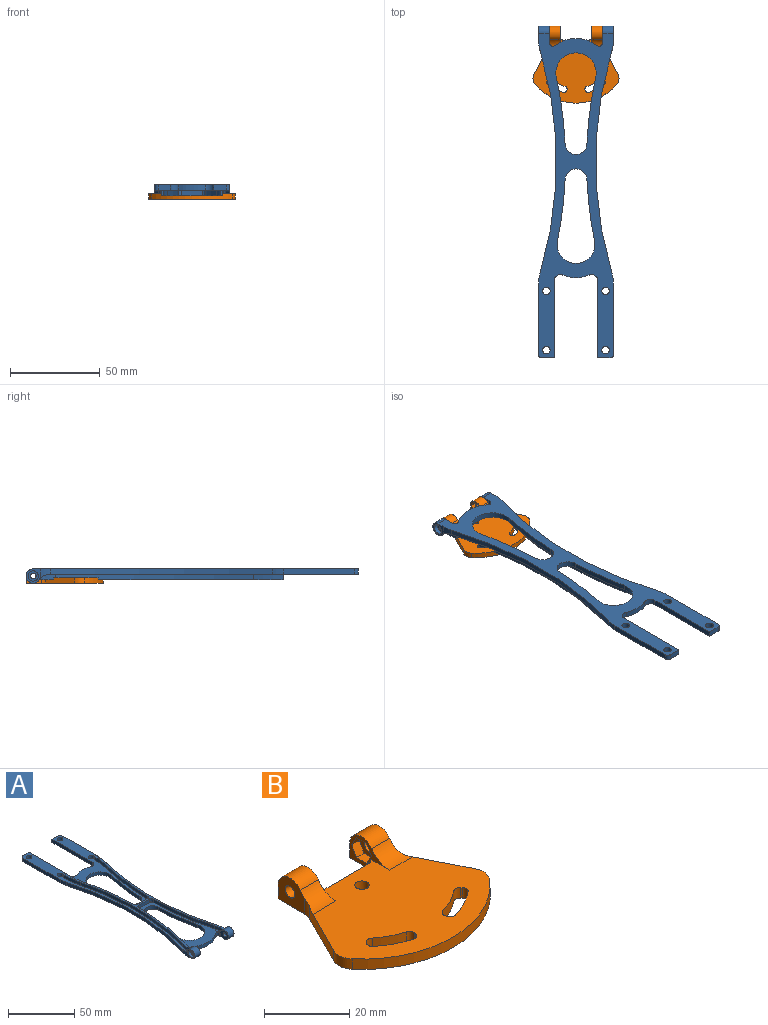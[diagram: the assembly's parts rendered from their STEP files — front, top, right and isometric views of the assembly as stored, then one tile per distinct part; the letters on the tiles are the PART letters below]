
ASSEMBLY  parts=2 mates=1
PART A: 78 faces, bbox 41.7x185x8 mm
  f0: plane 171.78x41.7mm, normal (0,0,1), area 1732.8mm2, adj f7,f8,f9,f10,f16,f17,f18,f19
  f1: plane 8x8mm, normal (-1,0,0), area 28.3mm2, adj f5,f10,f38,f43,f73
  f2: plane 13.22x8mm, normal (1,0,0), area 49.6mm2, adj f5,f6,f11,f38,f43,f71
  f3: plane 13.22x8mm, normal (-1,0,0), area 49.6mm2, adj f5,f6,f15,f37,f44,f68
  f4: plane 8x8mm, normal (1,0,0), area 28.3mm2, adj f5,f16,f37,f44,f70
  f5: plane 181x41.7mm, normal (0,0,-1), area 2806.4mm2, adj f1,f2,f3,f4,f7,f8,f9,f10
  f6: plane 67.94x33.25mm, normal (0,0,1), area 544.7mm2, adj f2,f3,f11,f12,f13,f14,f15,f31
  f7: cylinder r=6.08mm len=12.14mm, axis (0,0,-1), area 55.6mm2, adj f0,f5,f8,f36
  f8: cylinder r=218.83mm len=34.19mm, axis (0,0,-1), area 103.5mm2, adj f0,f5,f7,f9
  f9: cylinder r=10.53mm len=21.07mm, axis (0,0,-1), area 112.1mm2, adj f0,f5,f8,f36
  f10: cylinder r=20mm len=5.79mm, axis (0,0,-1), area 21.4mm2, adj f0,f1,f5,f34,f43
  f11: cylinder r=39.51mm len=3mm, axis (0,0,-1), area 4.1mm2, adj f2,f5,f6,f12
  f12: cylinder r=2mm len=3.21mm, axis (0,0,-1), area 13.1mm2, adj f5,f6,f11,f13
  f13: cylinder r=19.23mm len=23.27mm, axis (0,0,-1), area 75mm2, adj f5,f6,f12,f14
  f14: cylinder r=2mm len=3.21mm, axis (0,0,-1), area 13.1mm2, adj f5,f6,f13,f15
  f15: cylinder r=39.51mm len=3mm, axis (0,0,-1), area 4.1mm2, adj f3,f5,f6,f14
  f16: cylinder r=20mm len=5.79mm, axis (0,0,-1), area 21.4mm2, adj f0,f4,f5,f17,f44
  f17: cylinder r=213.83mm len=123.73mm, axis (0,0,-1), area 376.6mm2, adj f0,f5,f16,f18
  f18: cylinder r=20mm len=5.79mm, axis (0,0,-1), area 17.6mm2, adj f0,f5,f17,f19
  f19: plane 39.8x3mm, normal (1,0,0), area 119.4mm2, adj f0,f5,f18,f20
  f20: cylinder r=1.9mm len=3mm, axis (0,0,-1), area 9mm2, adj f0,f5,f19,f21
  f21: plane 6.8x3mm, normal (0,1,0), area 20.4mm2, adj f0,f5,f20,f22
  f22: plane 42.97x3mm, normal (-1,0,0), area 128.9mm2, adj f0,f5,f21,f23
  f23: cylinder r=3.5mm len=4.87mm, axis (0,0,-1), area 20.7mm2, adj f0,f5,f22,f24
  f24: cylinder r=18.53mm len=14.55mm, axis (0,0,-1), area 44.9mm2, adj f0,f5,f23,f25
  f25: cylinder r=3.5mm len=4.87mm, axis (0,0,-1), area 20.7mm2, adj f0,f5,f24,f26
  f26: plane 42.97x3mm, normal (1,0,0), area 128.9mm2, adj f0,f5,f25,f27
  f27: plane 6.8x3mm, normal (0,1,0), area 20.4mm2, adj f0,f5,f26,f28
  f28: cylinder r=1.9mm len=3mm, axis (0,0,-1), area 9mm2, adj f0,f5,f27,f29
  f29: plane 39.8x3mm, normal (-1,0,0), area 119.4mm2, adj f0,f5,f28,f30
  f30: cylinder r=20mm len=5.79mm, axis (0,0,-1), area 17.6mm2, adj f0,f5,f29,f34
  f31: cylinder r=6.08mm len=12.14mm, axis (0,0,-1), area 55.6mm2, adj f5,f6,f32,f35
  f32: cylinder r=218.83mm len=37.24mm, axis (0,0,-1), area 112.8mm2, adj f5,f6,f31,f33
  f33: cylinder r=11.23mm len=22.46mm, axis (0,0,-1), area 120.4mm2, adj f5,f6,f32,f35
  f34: cylinder r=213.83mm len=123.73mm, axis (0,0,-1), area 376.6mm2, adj f0,f5,f10,f30
  f35: cylinder r=218.83mm len=37.24mm, axis (0,0,-1), area 112.8mm2, adj f5,f6,f31,f33
  f36: cylinder r=218.83mm len=34.19mm, axis (0,0,-1), area 103.5mm2, adj f0,f5,f7,f9
  f37: cylinder r=4mm len=8mm, axis (1,0,0), area 99mm2, adj f3,f4,f5,f44
  f38: cylinder r=4mm len=8mm, axis (1,0,0), area 99mm2, adj f1,f2,f5,f43
  f39: cylinder r=2.1mm len=4.2mm, axis (0,0,-1), area 39.6mm2, adj f0,f5
  f40: cylinder r=2.1mm len=4.2mm, axis (0,0,-1), area 39.6mm2, adj f0,f5
  f41: cylinder r=2.1mm len=4.2mm, axis (0,0,-1), area 39.6mm2, adj f0,f5
  f42: cylinder r=2.1mm len=4.2mm, axis (0,0,-1), area 39.6mm2, adj f0,f5
  f43: cylinder r=7mm len=5.99mm, axis (1,0,0), area 30.3mm2, adj f0,f1,f2,f6,f10,f38,f45,f46
  f44: cylinder r=7mm len=5.99mm, axis (1,0,0), area 30.3mm2, adj f0,f3,f4,f6,f16,f37,f47,f48
  f45: plane 0.66x0.53mm, normal (-1,0,0), area 0.2mm2, adj f43,f47,f61
  f46: plane 0.66x0.53mm, normal (1,0,0), area 0.2mm2, adj f43,f47,f64
  f47: plane 135.83x37.22mm, normal (0,0,1), area 438.3mm2, adj f43,f44,f45,f46,f48,f49,f50,f51
  f48: plane 0.66x0.53mm, normal (-1,0,0), area 0.2mm2, adj f44,f47,f53
  f49: plane 0.66x0.53mm, normal (1,0,0), area 0.2mm2, adj f44,f47,f56
  f50: cylinder r=217.08mm len=48.83mm, axis (0,0,1), area 148mm2, adj f0,f47,f54,f75
  f51: plane 3x1.5mm, normal (0,1,0), area 4.5mm2, adj f0,f47,f54,f57
  f52: cylinder r=217.08mm len=57.11mm, axis (0,0,1), area 173.7mm2, adj f6,f47,f53,f74
  f53: cylinder r=28.36mm len=7.82mm, axis (0,0,1), area 20mm2, adj f6,f44,f47,f48,f52
  f54: cylinder r=67.77mm len=16.09mm, axis (0,0,1), area 48.7mm2, adj f0,f47,f50,f51
  f55: cylinder r=215.58mm len=110.62mm, axis (0,0,1), area 335.7mm2, adj f0,f47,f56,f57
  f56: cylinder r=29.86mm len=8.23mm, axis (0,0,1), area 21.3mm2, adj f0,f44,f47,f49,f55
  f57: cylinder r=69.27mm len=16.45mm, axis (0,0,1), area 49.8mm2, adj f0,f47,f51,f55
  f58: cylinder r=217.08mm len=48.83mm, axis (0,0,1), area 148mm2, adj f0,f47,f65,f77
  f59: plane 3x1.5mm, normal (0,1,0), area 4.5mm2, adj f0,f47,f62,f65
  f60: cylinder r=215.58mm len=110.62mm, axis (0,0,1), area 335.7mm2, adj f0,f47,f61,f62
  f61: cylinder r=29.86mm len=8.23mm, axis (0,0,1), area 21.3mm2, adj f0,f43,f45,f47,f60
  f62: cylinder r=69.27mm len=16.45mm, axis (0,0,1), area 49.8mm2, adj f0,f47,f59,f60
  f63: cylinder r=217.08mm len=57.11mm, axis (0,0,1), area 173.7mm2, adj f6,f47,f64,f76
  f64: cylinder r=28.36mm len=7.82mm, axis (0,0,1), area 20mm2, adj f6,f43,f46,f47,f63
  f65: cylinder r=67.77mm len=16.09mm, axis (0,0,1), area 48.7mm2, adj f0,f47,f58,f59
  f66: plane 11.23x3mm, normal (0,-1,0), area 33.7mm2, adj f6,f47,f74,f76
  f67: plane 11.23x3mm, normal (0,1,0), area 33.7mm2, adj f0,f47,f75,f77
  f68: cylinder r=1.6mm len=3.49mm, axis (1,0,0), area 35mm2, adj f3,f69
  f69: plane 5.7x5.7mm, normal (1,0,0), area 17.5mm2, adj f68,f70
  f70: cylinder r=2.85mm len=5.7mm, axis (1,0,0), area 44.8mm2, adj f4,f69
  f71: cylinder r=1.6mm len=3.49mm, axis (1,0,0), area 35mm2, adj f2,f72
  f72: plane 5.7x5.7mm, normal (-1,0,0), area 17.5mm2, adj f71,f73
  f73: cylinder r=2.85mm len=5.7mm, axis (-1,0,0), area 44.8mm2, adj f1,f72
  f74: cylinder r=2mm len=3mm, axis (0,0,1), area 9.3mm2, adj f6,f47,f52,f66
  f75: cylinder r=2mm len=3mm, axis (0,0,1), area 9.3mm2, adj f0,f47,f50,f67
  f76: cylinder r=2mm len=3mm, axis (0,0,1), area 9.3mm2, adj f6,f47,f63,f66
  f77: cylinder r=2mm len=3mm, axis (0,0,1), area 9.3mm2, adj f0,f47,f58,f67
PART B: 57 faces, bbox 48.1x43.1x8.1 mm
  f0: cylinder r=1.6mm len=3.49mm, axis (1,0,0), area 35mm2, adj f17,f44
  f1: cylinder r=1.6mm len=3.49mm, axis (1,0,0), area 35mm2, adj f23,f37
  f2: plane 48.05x36.41mm, normal (0,0,1), area 1147.8mm2, adj f3,f4,f5,f6,f7,f8,f9,f10
  f3: cylinder r=1.5mm len=3mm, axis (0,0,-1), area 6.8mm2, adj f2,f4,f30,f31
  f4: cylinder r=21.6mm len=7.49mm, axis (0,0,-1), area 25.5mm2, adj f2,f3,f5,f31
  f5: cylinder r=1.5mm len=3mm, axis (0,0,-1), area 6.8mm2, adj f2,f4,f6,f31
  f6: plane 3x0.3mm, normal (-0.74,-0.68,0), area 1.2mm2, adj f2,f5,f7,f31
  f7: cylinder r=1.5mm len=3mm, axis (0,0,-1), area 7.4mm2, adj f2,f6,f8,f31
  f8: cylinder r=25mm len=8.72mm, axis (0,0,-1), area 29.7mm2, adj f2,f7,f9,f31
  f9: cylinder r=1.5mm len=3mm, axis (0,0,-1), area 7.4mm2, adj f2,f8,f30,f31
  f10: cylinder r=1.5mm len=3mm, axis (0,0,-1), area 6.8mm2, adj f2,f11,f28,f31
  f11: cylinder r=21.6mm len=7.49mm, axis (0,0,-1), area 25.5mm2, adj f2,f10,f12,f31
  f12: cylinder r=1.5mm len=3mm, axis (0,0,-1), area 6.8mm2, adj f2,f11,f13,f31
  f13: plane 3x0.39mm, normal (-0.98,0.22,0), area 1.2mm2, adj f2,f12,f14,f31
  f14: cylinder r=1.5mm len=3mm, axis (0,0,-1), area 7.4mm2, adj f2,f13,f15,f31
  f15: cylinder r=25mm len=8.72mm, axis (0,0,-1), area 29.7mm2, adj f2,f14,f16,f31
  f16: cylinder r=1.5mm len=3mm, axis (0,0,-1), area 7.4mm2, adj f2,f15,f28,f31
  f17: plane 8.81x8mm, normal (-1,0,0), area 53.2mm2, adj f0,f29,f31,f33,f34,f55
  f18: plane 15.98x8.07mm, normal (-0.89,0.45,0), area 53.9mm2, adj f2,f19,f31,f34,f55
  f19: cylinder r=5mm len=5.51mm, axis (0,0,-1), area 17.7mm2, adj f2,f18,f20,f31
  f20: cylinder r=30mm len=45.52mm, axis (0,0,-1), area 155mm2, adj f2,f19,f21,f31
  f21: cylinder r=5mm len=5.51mm, axis (0,0,-1), area 17.7mm2, adj f2,f20,f22,f31
  f22: plane 15.98x8.07mm, normal (0.89,0.45,0), area 53.9mm2, adj f2,f21,f31,f35,f56
  f23: plane 8.81x8mm, normal (1,0,0), area 53.2mm2, adj f1,f24,f31,f32,f35,f56
  f24: plane 5.99x4mm, normal (0,1,0), area 23.9mm2, adj f23,f25,f31,f32
  f25: plane 13.22x8mm, normal (-1,0,0), area 27.3mm2, adj f2,f24,f31,f32,f35,f38,f39,f40
  f26: plane 13.9x3mm, normal (0,1,0), area 41.2mm2, adj f2,f31,f51,f52,f53,f54
  f27: plane 13.22x8mm, normal (1,0,0), area 27.3mm2, adj f2,f29,f31,f33,f34,f45,f46,f47
  f28: plane 3x0.3mm, normal (0.74,-0.68,0), area 1.2mm2, adj f2,f10,f16,f31
  f29: plane 5.99x4mm, normal (0,1,0), area 23.9mm2, adj f17,f27,f31,f33
  f30: plane 3x0.39mm, normal (0.98,0.22,0), area 1.2mm2, adj f2,f3,f9,f31
  f31: plane 47.94x43mm, normal (0,0,-1), area 1311.9mm2, adj f3,f4,f5,f6,f7,f8,f9,f10
  f32: cylinder r=4mm len=7.35mm, axis (1,0,0), area 61.4mm2, adj f23,f24,f25,f35
  f33: cylinder r=4mm len=7.35mm, axis (1,0,0), area 61.4mm2, adj f17,f27,f29,f34
  f34: cylinder r=7mm len=7.61mm, axis (1,0,0), area 44.7mm2, adj f2,f17,f18,f27,f33,f55
  f35: cylinder r=7mm len=7.61mm, axis (1,0,0), area 44.7mm2, adj f2,f22,f23,f25,f32,f56
  f36: cylinder r=1.7mm len=3.4mm, axis (0,0,-1), area 32mm2, adj f2,f31
  f37: plane 6.58x5.7mm, normal (-1,0,0), area 20.1mm2, adj f1,f38,f39,f40,f41,f42,f43
  f38: plane 2.87x2.52mm, normal (0,0.87,0.5), area 8.2mm2, adj f25,f37,f39,f43,f54
  f39: plane 3.29x2.5mm, normal (0,0,1), area 8.2mm2, adj f25,f37,f38,f40
  f40: plane 2.85x2.5mm, normal (0,-0.87,0.5), area 8.2mm2, adj f25,f37,f39,f41
  f41: plane 2.85x2.5mm, normal (0,-0.87,-0.5), area 8.2mm2, adj f25,f37,f40,f42
  f42: plane 3.29x2.5mm, normal (0,0,-1), area 8.2mm2, adj f25,f37,f41,f43
  f43: plane 2.85x2.5mm, normal (0,0.87,-0.5), area 8.2mm2, adj f25,f37,f38,f42
  f44: plane 6.58x5.7mm, normal (1,0,0), area 20.1mm2, adj f0,f45,f46,f47,f48,f49,f50
  f45: plane 2.85x2.5mm, normal (0,0.87,-0.5), area 8.2mm2, adj f27,f44,f46,f50
  f46: plane 3.29x2.5mm, normal (0,0,-1), area 8.2mm2, adj f27,f44,f45,f47
  f47: plane 2.85x2.5mm, normal (0,-0.87,-0.5), area 8.2mm2, adj f27,f44,f46,f48
  f48: plane 2.85x2.5mm, normal (0,-0.87,0.5), area 8.2mm2, adj f27,f44,f47,f49
  f49: plane 3.29x2.5mm, normal (0,0,1), area 8.2mm2, adj f27,f44,f48,f50
  f50: plane 2.87x2.52mm, normal (0,0.87,0.5), area 8.2mm2, adj f27,f44,f45,f49,f52
  f51: cylinder r=2mm len=2mm, axis (0,0,1), area 5.5mm2, adj f26,f27,f31,f52
  f52: bspline ~2.3x2.13mm, area 3.4mm2, adj f2,f26,f50,f51
  f53: cylinder r=2mm len=2mm, axis (0,0,-1), area 5.5mm2, adj f25,f26,f31,f54
  f54: bspline ~2.3x2.13mm, area 3.4mm2, adj f2,f26,f38,f53
  f55: cylinder r=5mm len=4.56mm, axis (0,0,1), area 9.2mm2, adj f17,f18,f31,f34
  f56: cylinder r=5mm len=4.56mm, axis (0,0,1), area 9.2mm2, adj f22,f23,f31,f35
PLACE A rot(axis=(-1,0,0),180deg) t=(-31.37,-281.81,-1.32)mm
PLACE B t=(-31.37,38.49,-9.32)mm fixed
MATE revolute B.f0 <-> A.f37  axis (1,0,0) through (-16.54,-121.66,-5.32)mm
